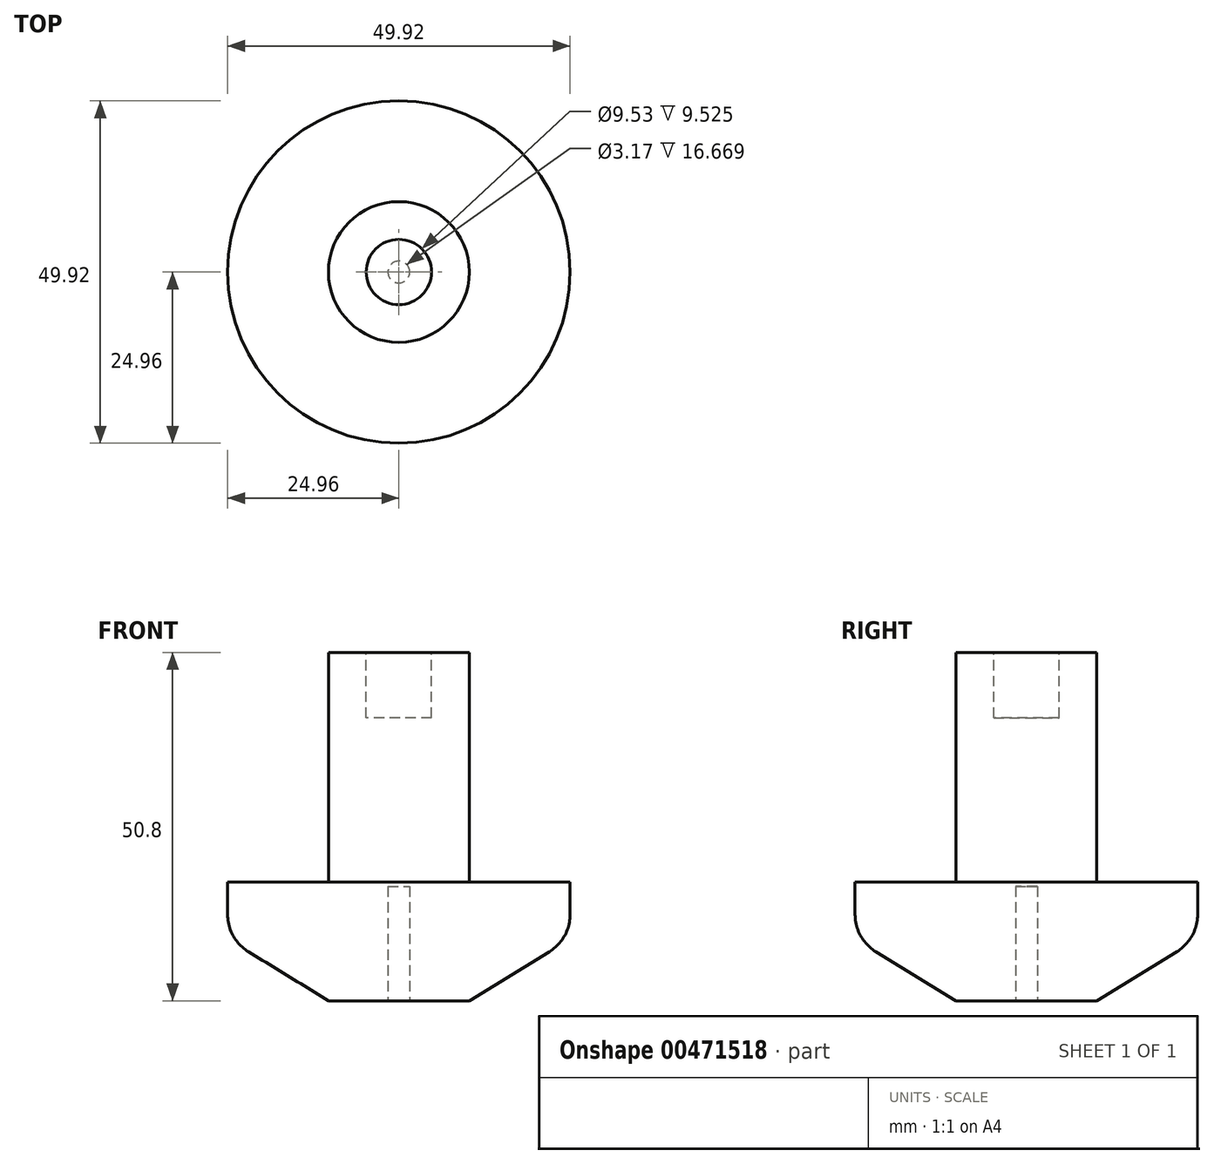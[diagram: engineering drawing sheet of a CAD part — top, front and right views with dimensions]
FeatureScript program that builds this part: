
annotation { "Feature Type Name" : "Feature", "Feature Type Description" : "" }
export const myFeature = defineFeature(function(context is Context, id is Id, definition is map)
    precondition{}
    {
        {
            var Q0;
            Q0=qCreatedBy(makeId("Front.planeOp"),FACE);
            var sketch = newSketch(context, id + "F0", { "sketchPlane" : qUnion([Q0])});
            skLineSegment(sketch, "E0", {"start": v(0, 0) * mm, "end": v(0, 50.8) * mm});
            skLineSegment(sketch, "E1", {"start": v(0, 0) * mm, "end": v(10.26, 0) * mm});
            skLineSegment(sketch, "E2", {"start": v(10.26, 0) * mm, "end": v(21.93, 7.15) * mm});
            skLineSegment(sketch, "E3", {"start": v(24.96, 12.57) * mm, "end": v(24.96, 17.33) * mm});
            skLineSegment(sketch, "E4", {"start": v(24.96, 17.33) * mm, "end": v(10.26, 17.33) * mm});
            skLineSegment(sketch, "E5", {"start": v(10.26, 17.33) * mm, "end": v(10.26, 50.8) * mm});
            skLineSegment(sketch, "E6", {"start": v(10.26, 50.8) * mm, "end": v(0, 50.8) * mm});
            skPoint(sketch, "E7.visualSharp", {"position": v(24.96, 9.01) * mm});
            skArc(sketch, "E7.filletArc", {"start": v(21.93, 7.15) * mm, "mid": v(24.15, 9.47) * mm, "end": v(24.96, 12.57) * mm});
            skSolve(sketch);
        }
        {
            var Q0;
            Q0=makeQuery(id+"F0.imprint","IMPRINT",FACE,{"disambiguationData":[TD([[makeQuery(id+"F0.imprint","IMPRINT",EDGE,{"derivedFrom":sQuery(id+"F0.wireOp",EDGE,"E0")}),-1.0]])]});
            var Q1;
            Q1=sQuery(id+"F0.wireOp",EDGE,"E0");
            revolve(context, id + "F1", {"entities" : qUnion([Q0]), "axis" : qUnion([Q1]), "revolveType" : RevolveType.FULL});
        }
        {
            var Q0;
            Q0=makeQuery(id+"F1.opRevolve","SWEPT_FACE",FACE,{"disambiguationData":[OSD([sQuery(id+"F0.wireOp",EDGE,"E6")])]});
            var sketch = newSketch(context, id + "F2", { "sketchPlane" : qUnion([Q0])});
            skCircle(sketch, "E8", {"center": v(0, 0) * mm, "radius": 4.76 * mm});
            skSolve(sketch);
        }
        {
            var Q0;
            Q0=makeQuery(id+"F2.imprint","IMPRINT",FACE,{"disambiguationData":[TD([[makeQuery(id+"F2.imprint","IMPRINT",EDGE,{"derivedFrom":sQuery(id+"F2.wireOp",EDGE,"E8")}),1.0]])]});
            extrude(context, id + "F3", {"entities" : qUnion([Q0]), "operationType" : NewBodyOperationType.REMOVE, "oppositeDirection" : true, "depth" : 9.52 * mm});
        }
        {
            var Q0;
            Q0=makeQuery(id+"F1.opRevolve","SWEPT_FACE",FACE,{"disambiguationData":[OSD([sQuery(id+"F0.wireOp",EDGE,"E1")])]});
            var sketch = newSketch(context, id + "F4", { "sketchPlane" : qUnion([Q0])});
            skCircle(sketch, "E9", {"center": v(0, 0) * mm, "radius": 1.59 * mm});
            skSolve(sketch);
        }
        {
            var Q0;
            Q0 = qSketchRegion(id + "F4", true);
            extrude(context, id + "F5", {"entities" : qUnion([Q0]), "operationType" : NewBodyOperationType.REMOVE, "oppositeDirection" : true, "depth" : 16.67 * mm});
        }
    });
